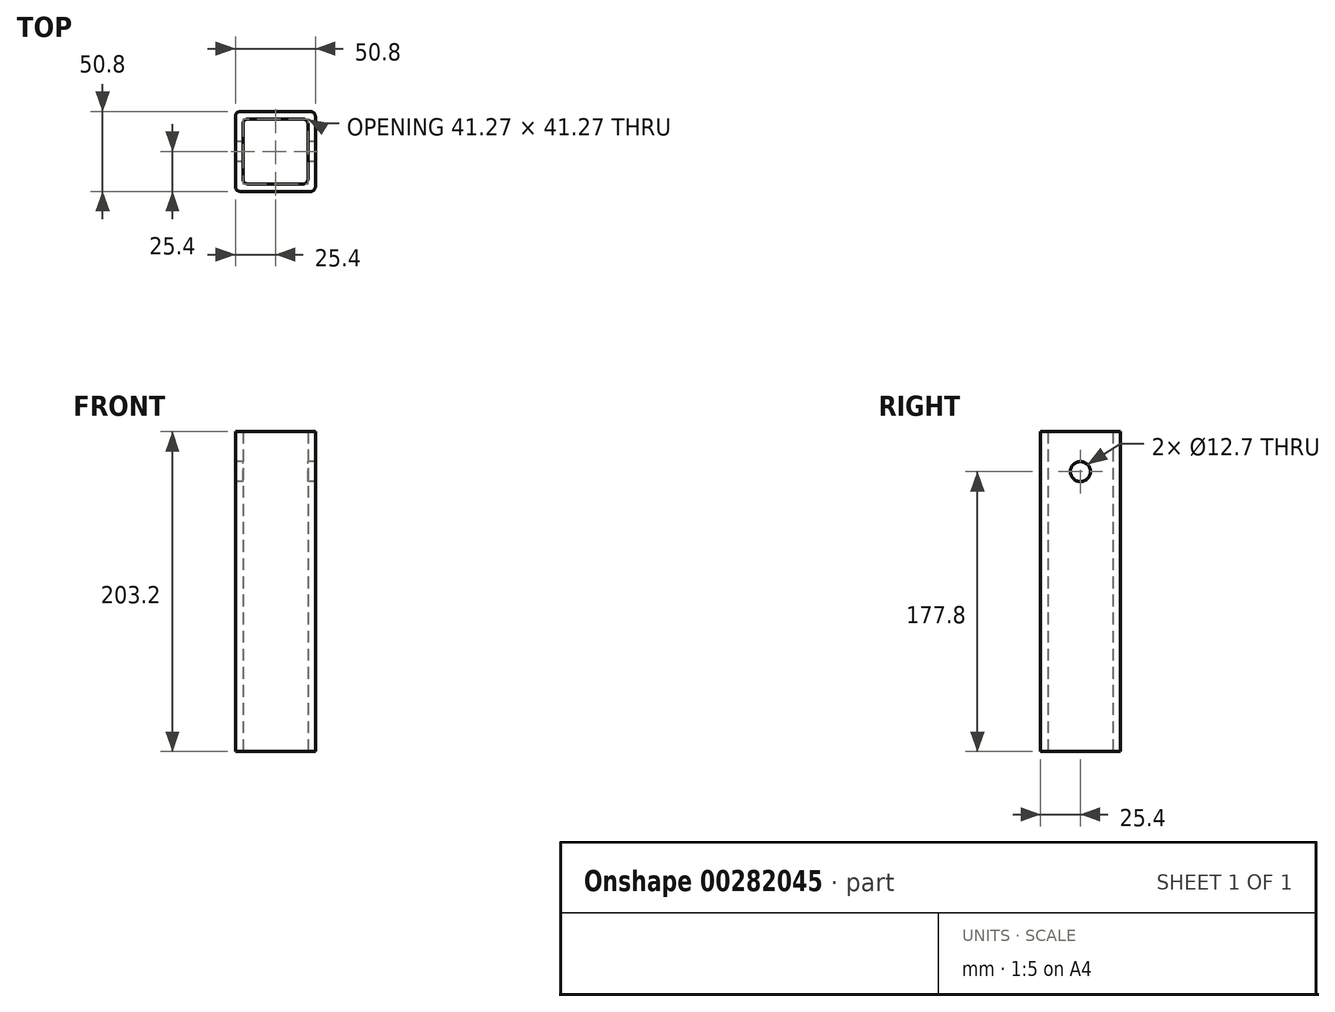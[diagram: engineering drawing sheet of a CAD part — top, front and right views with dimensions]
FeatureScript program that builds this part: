
annotation { "Feature Type Name" : "Feature", "Feature Type Description" : "" }
export const myFeature = defineFeature(function(context is Context, id is Id, definition is map)
    precondition{}
    {
        {
            var Q0;
            Q0=qCreatedBy(makeId("Top.planeOp"),FACE);
            var sketch = newSketch(context, id + "F0", { "sketchPlane" : qUnion([Q0])});
            skLineSegment(sketch, "E0.bottom", {"start": v(17.46, 20.64) * mm, "end": v(-17.46, 20.64) * mm});
            skLineSegment(sketch, "E0.top", {"start": v(17.46, -20.64) * mm, "end": v(-17.46, -20.64) * mm});
            skLineSegment(sketch, "E0.left", {"start": v(20.64, 17.46) * mm, "end": v(20.64, -17.46) * mm});
            skLineSegment(sketch, "E0.right", {"start": v(-20.64, 17.46) * mm, "end": v(-20.64, -17.46) * mm});
            skPoint(sketch, "E0.middle", {"position": v(0, 0) * mm});
            skLineSegment(sketch, "E1.bottom", {"start": v(22.22, 25.4) * mm, "end": v(-22.23, 25.4) * mm});
            skLineSegment(sketch, "E1.top", {"start": v(22.22, -25.4) * mm, "end": v(-22.22, -25.4) * mm});
            skLineSegment(sketch, "E1.left", {"start": v(25.4, 22.22) * mm, "end": v(25.4, -22.22) * mm});
            skLineSegment(sketch, "E1.right", {"start": v(-25.4, 22.23) * mm, "end": v(-25.4, -22.22) * mm});
            skPoint(sketch, "E2.visualSharp", {"position": v(-20.64, 20.64) * mm});
            skArc(sketch, "E2.filletArc", {"start": v(-17.46, 20.64) * mm, "mid": v(-19.7, 19.7) * mm, "end": v(-20.64, 17.46) * mm});
            skPoint(sketch, "E3.visualSharp", {"position": v(-25.4, 25.4) * mm});
            skArc(sketch, "E3.filletArc", {"start": v(-22.23, 25.4) * mm, "mid": v(-24.47, 24.47) * mm, "end": v(-25.4, 22.23) * mm});
            skPoint(sketch, "E4.visualSharp", {"position": v(-25.4, -25.4) * mm});
            skArc(sketch, "E4.filletArc", {"start": v(-25.4, -22.22) * mm, "mid": v(-24.47, -24.47) * mm, "end": v(-22.22, -25.4) * mm});
            skPoint(sketch, "E5.visualSharp", {"position": v(25.4, 25.4) * mm});
            skArc(sketch, "E5.filletArc", {"start": v(25.4, 22.22) * mm, "mid": v(24.47, 24.47) * mm, "end": v(22.22, 25.4) * mm});
            skPoint(sketch, "E6.visualSharp", {"position": v(25.4, -25.4) * mm});
            skArc(sketch, "E6.filletArc", {"start": v(22.22, -25.4) * mm, "mid": v(24.47, -24.47) * mm, "end": v(25.4, -22.22) * mm});
            skPoint(sketch, "E7.visualSharp", {"position": v(20.64, 20.64) * mm});
            skArc(sketch, "E7.filletArc", {"start": v(20.64, 17.46) * mm, "mid": v(19.7, 19.7) * mm, "end": v(17.46, 20.64) * mm});
            skPoint(sketch, "E8.visualSharp", {"position": v(-20.64, -20.64) * mm});
            skArc(sketch, "E8.filletArc", {"start": v(-20.64, -17.46) * mm, "mid": v(-19.7, -19.7) * mm, "end": v(-17.46, -20.64) * mm});
            skPoint(sketch, "E9.visualSharp", {"position": v(20.64, -20.64) * mm});
            skArc(sketch, "E9.filletArc", {"start": v(17.46, -20.64) * mm, "mid": v(19.7, -19.7) * mm, "end": v(20.64, -17.46) * mm});
            skSolve(sketch);
        }
        {
            var Q0;
            Q0 = qSketchRegion(id + "F0", true);
            extrude(context, id + "F1", {"entities" : qUnion([Q0]), "depth" : 203.2 * mm});
        }
        {
            var Q0;
            Q0=makeQuery(id+"F1.opExtrude","SWEPT_FACE",FACE,{"disambiguationData":[OSD([sQuery(id+"F0.wireOp",EDGE,"E1.right")])]});
            var sketch = newSketch(context, id + "F2", { "sketchPlane" : qUnion([Q0])});
            skCircle(sketch, "E10", {"center": v(0, 177.8) * mm, "radius": 6.35 * mm});
            skSolve(sketch);
        }
        {
            var Q0;
            Q0 = qSketchRegion(id + "F2", true);
            extrude(context, id + "F3", {"entities" : qUnion([Q0]), "operationType" : NewBodyOperationType.REMOVE, "endBound" : BoundingType.THROUGH_ALL, "oppositeDirection" : true, "depth" : 25.4 * mm});
        }
    });
